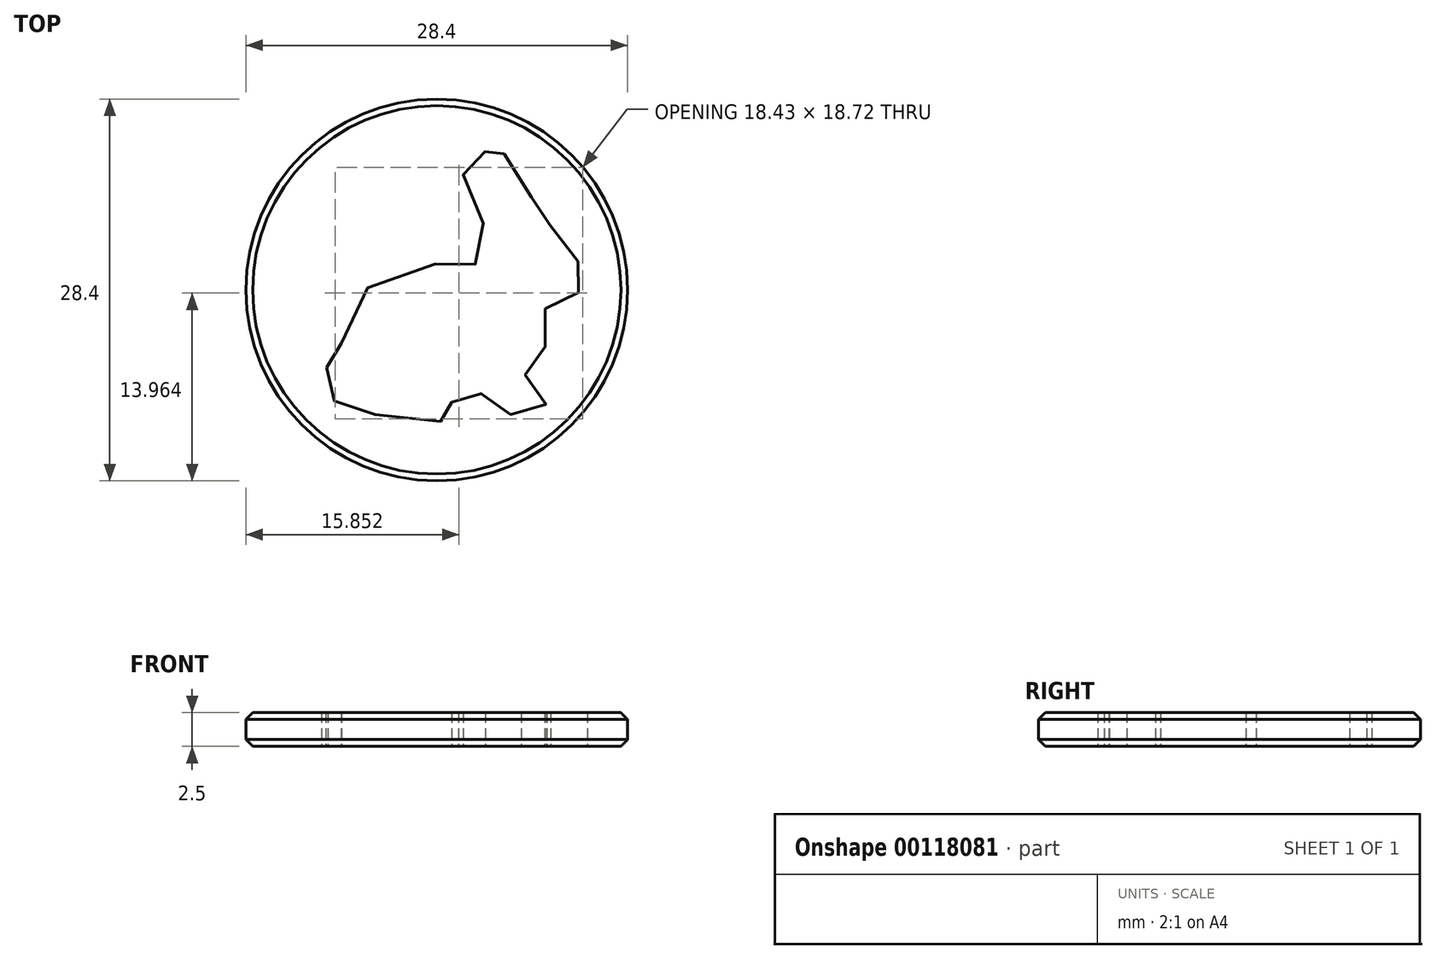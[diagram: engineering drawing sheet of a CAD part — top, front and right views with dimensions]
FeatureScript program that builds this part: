
annotation { "Feature Type Name" : "Feature", "Feature Type Description" : "" }
export const myFeature = defineFeature(function(context is Context, id is Id, definition is map)
    precondition{}
    {
        {
            var Q0;
            Q0=qCreatedBy(makeId("Top.planeOp"),FACE);
            var sketch = newSketch(context, id + "F0", { "sketchPlane" : qUnion([Q0])});
            skCircle(sketch, "E0", {"center": v(0, 0) * mm, "radius": 14.2 * mm});
            skFitSpline(sketch, "E1", {"points": [v(7.05, 6.88) * mm, v(6.34, 8.94) * mm, v(5.76, 10.02) * mm, v(5.62, 10.17) * mm, v(5.3, 10.2) * mm, v(4.86, 10.07) * mm, v(4.75, 9.88) * mm, v(4.7, 9.13) * mm, v(4.63, 8.93) * mm, v(4.48, 9.03) * mm, v(3.85, 9.95) * mm, v(3.29, 10.45) * mm, v(2.54, 10.59) * mm, v(2.2, 10.44) * mm, v(2, 10.14) * mm, v(1.98, 9.16) * mm, v(1.97, 8) * mm, v(2.11, 7) * mm, v(2.77, 5.93) * mm, v(3.37, 5.11) * mm, v(3.5, 4.86) * mm, v(3.6, 4.4) * mm, v(3.53, 2.5) * mm, v(3.4, 2.13) * mm, v(3.22, 2) * mm, v(2.9, 1.92) * mm, v(2.42, 1.57) * mm, v(2.16, 1.3) * mm, v(1.98, 1.2) * mm, v(1.76, 1.33) * mm, v(0.86, 1.74) * mm, v(-0.9, 1.97) * mm, v(-2.86, 1.67) * mm, v(-3.92, 1.15) * mm, v(-5.97, -0.6) * mm, v(-6.52, -1.35) * mm, v(-6.94, -2.52) * mm, v(-7.09, -3.86) * mm, v(-7.1, -5.24) * mm, v(-7.13, -5.48) * mm, v(-7.39, -5.47) * mm, v(-7.66, -5.17) * mm, v(-7.91, -5.17) * mm, v(-8.23, -5.89) * mm, v(-8.24, -6.3) * mm, v(-8.1, -6.58) * mm, v(-8.29, -6.7) * mm, v(-8.57, -7.13) * mm, v(-8.12, -7.8) * mm, v(-7.2, -8.6) * mm, v(-6.63, -8.9) * mm, v(-6.26, -8.97) * mm, v(-5.68, -8.95) * mm, v(-5.06, -9.07) * mm, v(-4.14, -9.42) * mm, v(-2.93, -9.56) * mm, v(-1.25, -9.68) * mm, v(0.45, -9.78) * mm, v(1.1, -9.72) * mm, v(1.44, -9.49) * mm, v(1.6, -9.3) * mm, v(1.56, -9.02) * mm, v(1.4, -8.8) * mm, v(1.16, -8.47) * mm, v(1.14, -8.28) * mm, v(1.4, -8.13) * mm, v(1.74, -8.1) * mm, v(2.04, -8.06) * mm, v(2.32, -7.9) * mm, v(2.94, -7.67) * mm, v(3.22, -7.66) * mm, v(3.43, -7.84) * mm, v(3.62, -8.04) * mm, v(3.82, -8.2) * mm, v(4.11, -8.35) * mm, v(4.79, -8.82) * mm, v(5.34, -9.17) * mm, v(5.57, -9.28) * mm, v(6, -9.32) * mm, v(7.2, -9.26) * mm, v(7.87, -9.1) * mm, v(8.17, -8.9) * mm, v(8.15, -8.55) * mm, v(7.68, -8.18) * mm, v(6.72, -7.55) * mm, v(6.43, -7.3) * mm, v(6.28, -6.9) * mm, v(6.41, -6.48) * mm, v(6.8, -6.22) * mm, v(7.18, -6.14) * mm, v(7.56, -5.98) * mm, v(7.86, -5.6) * mm, v(8.04, -4.89) * mm, v(8.07, -4.26) * mm, v(8.29, -3.71) * mm, v(8.42, -3.08) * mm, v(8.47, -2.3) * mm, v(8.32, -1.9) * mm, v(8.1, -1.59) * mm, v(8.1, -1.27) * mm, v(8.3, -1.02) * mm, v(8.88, -0.93) * mm, v(9.75, -0.73) * mm, v(10.07, -0.63) * mm, v(10.33, -0.44) * mm, v(10.96, 0.36) * mm, v(11.16, 0.65) * mm, v(11.22, 1.07) * mm, v(11.1, 1.44) * mm, v(10.89, 1.74) * mm, v(10.63, 1.9) * mm, v(10.3, 2.57) * mm, v(10.01, 3.06) * mm, v(9.4, 4) * mm, v(9.07, 4.45) * mm, v(8.52, 4.75) * mm, v(7.93, 4.92) * mm, v(7.37, 4.96) * mm, v(7.28, 5.02) * mm, v(7.24, 5.2) * mm, v(7.18, 6.24) * mm, v(7.05, 6.88) * mm]});
            skSolve(sketch);
        }
        {
            var Q0;
            Q0=makeQuery(id+"F0.imprint","IMPRINT",FACE,{"disambiguationData":[TD([[makeQuery(id+"F0.imprint","IMPRINT",EDGE,{"derivedFrom":sQuery(id+"F0.wireOp",EDGE,"E0")}),1.0]])]});
            extrude(context, id + "F1", {"entities" : qUnion([Q0]), "depth" : 2.5 * mm});
        }
        {
            var Q0;
            Q0=makeQuery(id+"F1.opExtrude","CAP_EDGE",EDGE,{"disambiguationData":[OSD([sQuery(id+"F0.wireOp",EDGE,"E0")])],"isStart":true});
            var Q1;
            Q1=makeQuery(id+"F1.opExtrude","CAP_EDGE",EDGE,{"disambiguationData":[OSD([sQuery(id+"F0.wireOp",EDGE,"E0")])],"isStart":false});
            chamfer(context, id + "F2", {"entities" : qUnion([Q0, Q1]), "width" : .5 * mm, "tangentPropagation" : true});
        }
    });
